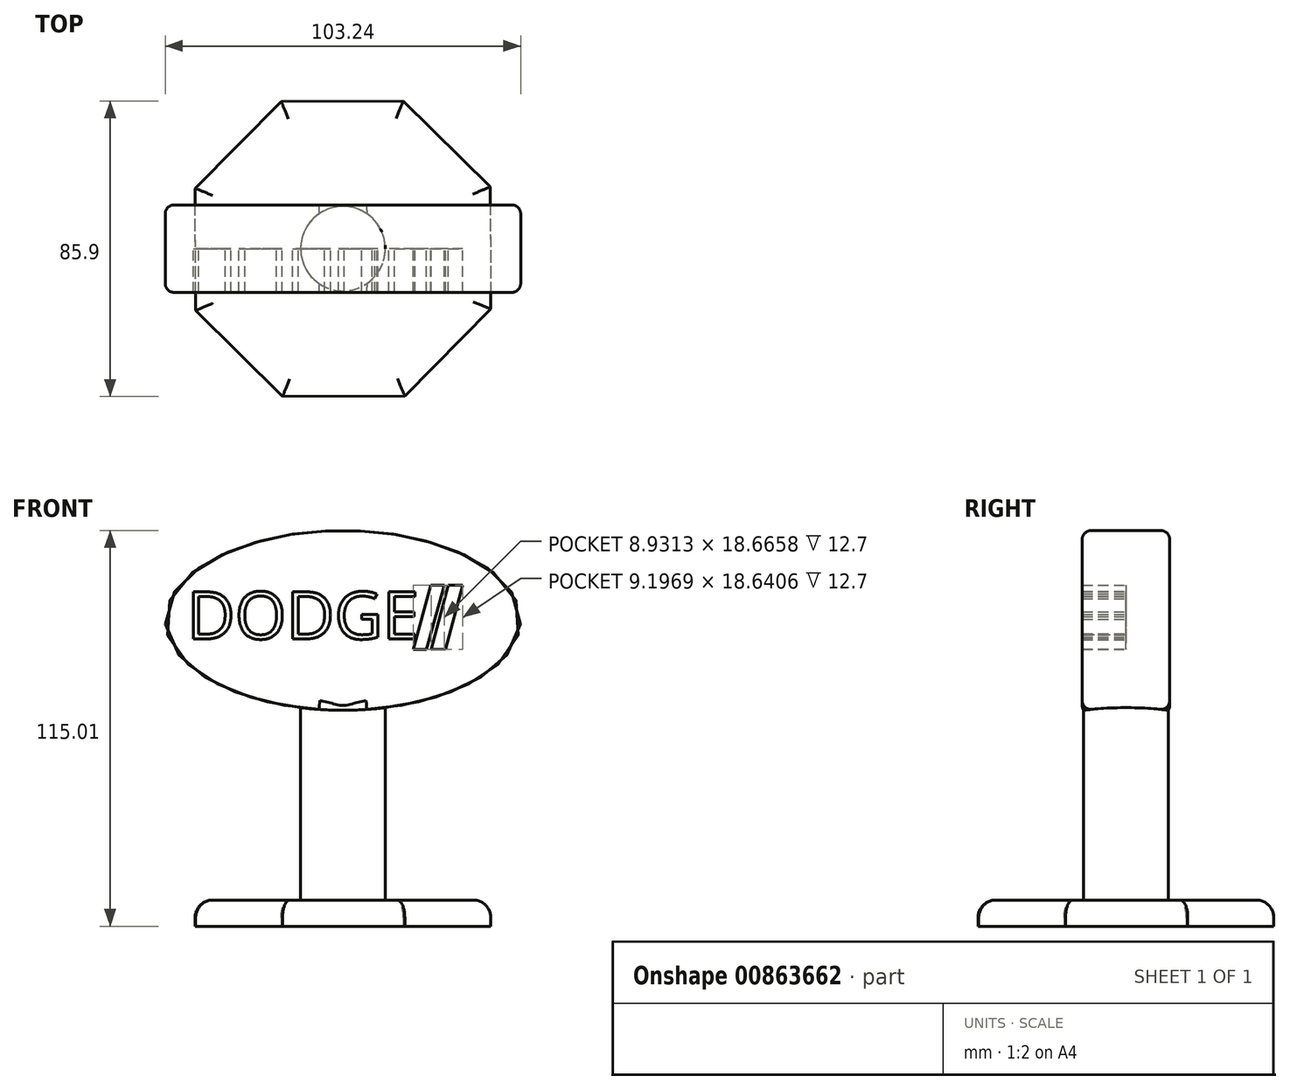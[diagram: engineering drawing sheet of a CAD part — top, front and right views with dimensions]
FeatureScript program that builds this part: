
annotation { "Feature Type Name" : "Feature", "Feature Type Description" : "" }
export const myFeature = defineFeature(function(context is Context, id is Id, definition is map)
    precondition{}
    {
        {
            var Q0;
            Q0=qCreatedBy(makeId("Top.planeOp"),FACE);
            var sketch = newSketch(context, id + "F0", { "sketchPlane" : qUnion([Q0])});
            skCircle(sketch, "E0.cCircle", {"center": v(0, 0) * mm, "radius": 42.86 * mm, "construction": true});
            skLineSegment(sketch, "E0.0", {"start": v(-42.95, 17.55) * mm, "end": v(-17.96, 42.78) * mm});
            skLineSegment(sketch, "E0.1", {"start": v(-17.96, 42.78) * mm, "end": v(17.55, 42.95) * mm});
            skLineSegment(sketch, "E0.2", {"start": v(17.55, 42.95) * mm, "end": v(42.78, 17.96) * mm});
            skLineSegment(sketch, "E0.3", {"start": v(42.78, 17.96) * mm, "end": v(42.95, -17.55) * mm});
            skLineSegment(sketch, "E0.4", {"start": v(42.95, -17.55) * mm, "end": v(17.96, -42.78) * mm});
            skLineSegment(sketch, "E0.5", {"start": v(17.96, -42.78) * mm, "end": v(-17.55, -42.95) * mm});
            skLineSegment(sketch, "E0.6", {"start": v(-17.55, -42.95) * mm, "end": v(-42.78, -17.96) * mm});
            skLineSegment(sketch, "E0.7", {"start": v(-42.78, -17.96) * mm, "end": v(-42.95, 17.55) * mm});
            skPoint(sketch, "E0.0.midPoint", {"position": v(-30.45, 30.16) * mm});
            skSolve(sketch);
        }
        {
            var Q0;
            Q0 = qSketchRegion(id + "F0", true);
            extrude(context, id + "F1", {"entities" : qUnion([Q0]), "depth" : 7.62 * mm, "offsetDistance" : 25.4 * mm});
        }
        {
            var Q0;
            Q0=qCreatedBy(makeId("Top.planeOp"),FACE);
            var sketch = newSketch(context, id + "F2", { "sketchPlane" : qUnion([Q0])});
            skCircle(sketch, "E1", {"center": v(0, 0) * mm, "radius": 12.3 * mm});
            skSolve(sketch);
        }
        {
            var Q0;
            Q0 = qSketchRegion(id + "F2", true);
            extrude(context, id + "F3", {"entities" : qUnion([Q0]), "operationType" : NewBodyOperationType.ADD, "depth" : 76.2 * mm, "offsetDistance" : 25.4 * mm});
        }
        {
            var Q0;
            Q0=qCreatedBy(makeId("Front.planeOp"),FACE);
            var sketch = newSketch(context, id + "F4", { "sketchPlane" : qUnion([Q0])});
            skEllipse(sketch, "E2", {"center": v(0, 88.9) * mm, "majorRadius": 51.62 * mm, "minorRadius": 26.1 * mm, "majorAxis": v(-1, 0)});
            skSolve(sketch);
        }
        {
            var Q0;
            Q0 = qSketchRegion(id + "F4", true);
            extrude(context, id + "F5", {"entities" : qUnion([Q0]), "operationType" : NewBodyOperationType.ADD, "endBound" : BoundingType.SYMMETRIC, "depth" : 25.4 * mm, "offsetDistance" : 25.4 * mm});
        }
        {
            var Q0;
            Q0=qCreatedBy(makeId("Front.planeOp"),FACE);
            var sketch = newSketch(context, id + "F6", { "sketchPlane" : qUnion([Q0])});
            skText(sketch, "E3", { "text": "DODGE", "fontName": "OpenSans-Regular.ttf"});
            const initialGuessF6  = {"E3": [-0.04534, 0.08351, 1, 0, 0.0138]};
            skSetInitialGuess(sketch, initialGuessF6);
            skSolve(sketch);
        }
        {
            var Q0;
            Q0 = qSketchRegion(id + "F6", true);
            extrude(context, id + "F7", {"entities" : qUnion([Q0]), "operationType" : NewBodyOperationType.REMOVE, "endBound" : BoundingType.THROUGH_ALL, "depth" : 38.1 * mm, "offsetDistance" : 25.4 * mm});
        }
        {
            var Q0;
            Q0=qCreatedBy(makeId("Front.planeOp"),FACE);
            var sketch = newSketch(context, id + "F8", { "sketchPlane" : qUnion([Q0])});
            skLineSegment(sketch, "E4", {"start": v(20.5, 80.46) * mm, "end": v(25.47, 99.1) * mm});
            skLineSegment(sketch, "E5", {"start": v(25.47, 99.1) * mm, "end": v(29.42, 99.1) * mm});
            skLineSegment(sketch, "E6", {"start": v(29.42, 99.1) * mm, "end": v(24.18, 80.43) * mm});
            skLineSegment(sketch, "E7", {"start": v(24.18, 80.43) * mm, "end": v(20.5, 80.46) * mm});
            skLineSegment(sketch, "E8", {"start": v(30.6, 99.1) * mm, "end": v(25.62, 80.46) * mm});
            skLineSegment(sketch, "E9", {"start": v(30.6, 99.1) * mm, "end": v(34.82, 99.1) * mm});
            skLineSegment(sketch, "E10", {"start": v(34.82, 99.1) * mm, "end": v(29.88, 80.59) * mm});
            skLineSegment(sketch, "E11", {"start": v(29.88, 80.59) * mm, "end": v(25.62, 80.46) * mm});
            skSolve(sketch);
        }
        {
            var Q0;
            Q0 = qSketchRegion(id + "F8", true);
            extrude(context, id + "F9", {"entities" : qUnion([Q0]), "operationType" : NewBodyOperationType.REMOVE, "depth" : 38.1 * mm, "offsetDistance" : 25.4 * mm});
        }
        {
            var Q0;
            Q0=makeQuery(id+"F5.opExtrude","CAP_EDGE",EDGE,{"disambiguationData":[OSD([sQuery(id+"F4.wireOp",EDGE,"E2")])],"isStart":false});
            var Q1;
            Q1=makeQuery(id+"F5.opExtrude","CAP_EDGE",EDGE,{"disambiguationData":[OSD([sQuery(id+"F4.wireOp",EDGE,"E2")])],"isStart":true});
            fillet(context, id + "F10", {"entities" : qUnion([Q0, Q1]), "radius" : 2.54 * mm, "tangentPropagation" : true, "allowEdgeOverflow" : false});
        }
        {
            var Q0;
            Q0=makeQuery(id+"F1.opExtrude","CAP_EDGE",EDGE,{"disambiguationData":[OSD([sQuery(id+"F0.wireOp",EDGE,"E0.4")])],"isStart":false});
            var Q1;
            Q1=makeQuery(id+"F1.opExtrude","CAP_EDGE",EDGE,{"disambiguationData":[OSD([sQuery(id+"F0.wireOp",EDGE,"E0.5")])],"isStart":false});
            var Q2;
            Q2=makeQuery(id+"F1.opExtrude","CAP_EDGE",EDGE,{"disambiguationData":[OSD([sQuery(id+"F0.wireOp",EDGE,"E0.6")])],"isStart":false});
            var Q3;
            Q3=makeQuery(id+"F1.opExtrude","CAP_EDGE",EDGE,{"disambiguationData":[OSD([sQuery(id+"F0.wireOp",EDGE,"E0.7")])],"isStart":false});
            var Q4;
            Q4=makeQuery(id+"F1.opExtrude","CAP_EDGE",EDGE,{"disambiguationData":[OSD([sQuery(id+"F0.wireOp",EDGE,"E0.0")])],"isStart":false});
            var Q5;
            Q5=makeQuery(id+"F1.opExtrude","CAP_EDGE",EDGE,{"disambiguationData":[OSD([sQuery(id+"F0.wireOp",EDGE,"E0.1")])],"isStart":false});
            var Q6;
            Q6=makeQuery(id+"F1.opExtrude","CAP_EDGE",EDGE,{"disambiguationData":[OSD([sQuery(id+"F0.wireOp",EDGE,"E0.2")])],"isStart":false});
            var Q7;
            Q7=makeQuery(id+"F1.opExtrude","CAP_EDGE",EDGE,{"disambiguationData":[OSD([sQuery(id+"F0.wireOp",EDGE,"E0.3")])],"isStart":false});
            fillet(context, id + "F11", {"entities" : qUnion([Q0, Q1, Q2, Q3, Q4, Q5, Q6, Q7]), "radius" : 5.08 * mm, "tangentPropagation" : true, "allowEdgeOverflow" : false});
        }
    });
